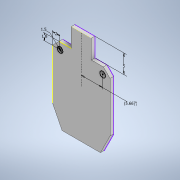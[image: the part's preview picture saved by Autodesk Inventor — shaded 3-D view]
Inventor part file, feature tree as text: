
AUTODESK INVENTOR PART (.ipt)
format: ipt  version: 2020 (Build 240168000, 168)  size: 119,296 bytes
history: native  units: in
note: dims shown in document units (in); Inventor stores cm internally (conversion verified against a paired STEP export)
features: extrude x2, sketch x2
ambient origin geometry x8: Origin, YZ Plane, XZ Plane, XY Plane, X Axis, Y Axis, Z Axis, Center Point
bodies: Solid1 (feature_tree)
feature tree (4):
  extrude  "Extrusion1"  Depth=0.375in TaperAngle=0.0deg
  extrude  "Extrusion2"  Depth=0.375in
  sketch  "Sketch1"  dims[d0=1.9685in d1=0.375in d2=0.0in]
  sketch  "Sketch2"  dims[d3=0.7087in d4=0.7874in d5=0.5906in d6=0.375in d7=0.0in d8=2.231in]
